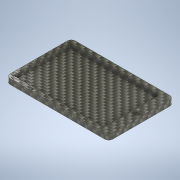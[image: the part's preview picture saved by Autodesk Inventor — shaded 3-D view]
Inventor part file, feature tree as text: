
AUTODESK INVENTOR PART (.ipt)
format: ipt  version: 2020 (Build 240168000, 168)  size: 166,912 bytes
history: native  units: in
note: dims shown in document units (in); Inventor stores cm internally (conversion verified against a paired STEP export)
features: extrude x5, sketch x1, fillet x1
ambient origin geometry x8: Origin, YZ Plane, XZ Plane, XY Plane, X Axis, Y Axis, Z Axis, Center Point
bodies: Solid1 (feature_tree)
feature tree (7):
  sketch  "Sketch1"  dims[d0=3.3701in d1=2.1252in d2=0.1252in d3=0.1252in d4=0.1575in d5=0.3543in d6=0.1969in d7=0.7874in d8=0.0787in d9=0.1181in d10=0.1969in d11=0.0in d12=0.0394in d13=0.0in d14=0.1969in d15=0.0in d16=0.1969in d17=0.0in d19=0.1575in d20=0.1181in d21=0.0in]
  extrude  "Extrusion1"  Depth=2.1252in
  extrude  "Extrusion2"  Depth=0.1252in
  extrude  "Extrusion3"  Depth=0.1252in
  extrude  "Extrusion4"  Depth=0.1575in
  fillet  "Fillet2"  Radius=0.3543in
  extrude  "Extrusion5"  Depth=0.1969in
